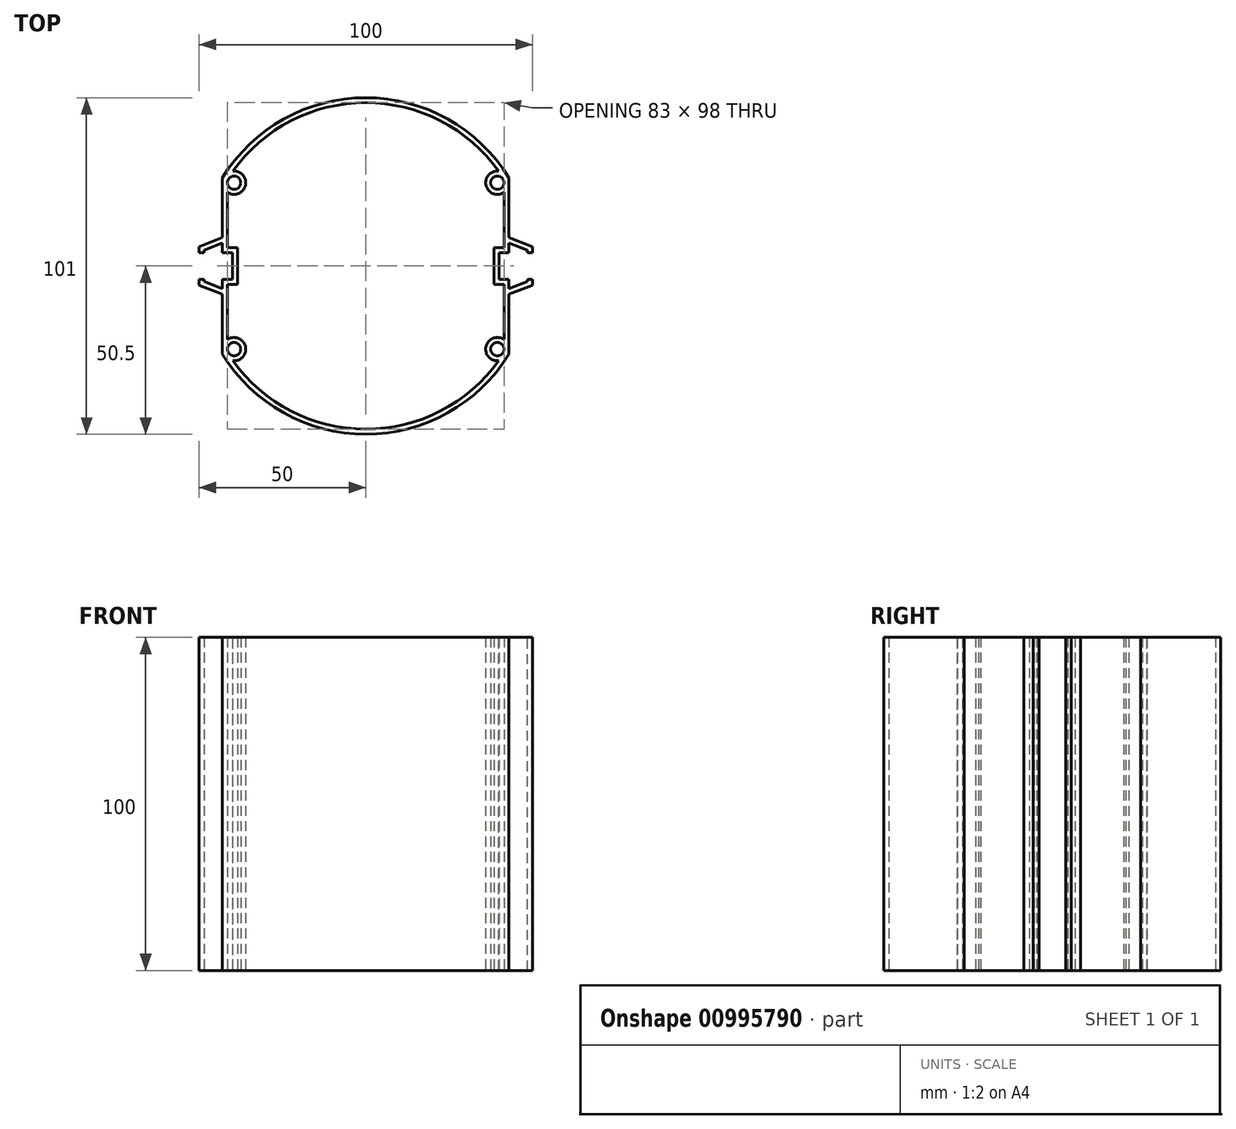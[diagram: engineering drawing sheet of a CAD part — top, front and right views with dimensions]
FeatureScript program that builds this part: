
annotation { "Feature Type Name" : "Feature", "Feature Type Description" : "" }
export const myFeature = defineFeature(function(context is Context, id is Id, definition is map)
    precondition{}
    {
        {
            var Q0;
            Q0=qCreatedBy(makeId("Top.planeOp"),FACE);
            var sketch = newSketch(context, id + "F0", { "sketchPlane" : qUnion([Q0])});
            skArc(sketch, "E0", {"start": v(43, 26.48) * mm, "mid": v(0, 50.5) * mm, "end": v(-43, 26.48) * mm});
            skArc(sketch, "E1", {"start": v(-43, -26.48) * mm, "mid": v(0, -50.5) * mm, "end": v(43, -26.48) * mm});
            skCircle(sketch, "E2", {"center": v(39.5, 24.98) * mm, "radius": 2 * mm});
            skCircle(sketch, "E3", {"center": v(-39.5, 24.98) * mm, "radius": 2 * mm});
            skCircle(sketch, "E4", {"center": v(-39.5, -24.98) * mm, "radius": 2 * mm});
            skCircle(sketch, "E5", {"center": v(39.5, -24.98) * mm, "radius": 2 * mm});
            skLineSegment(sketch, "E6.bottom", {"start": v(40, 4) * mm, "end": v(52, 4) * mm});
            skLineSegment(sketch, "E6.top", {"start": v(40, -4) * mm, "end": v(52, -4) * mm});
            skLineSegment(sketch, "E6.left", {"start": v(40, 4) * mm, "end": v(40, -4) * mm});
            skLineSegment(sketch, "E6.right", {"start": v(52, 4) * mm, "end": v(52, -4) * mm});
            skLineSegment(sketch, "E7", {"start": v(43, 26.48) * mm, "end": v(43, 4) * mm});
            skLineSegment(sketch, "E8", {"start": v(43, -26.48) * mm, "end": v(43, -4) * mm});
            skLineSegment(sketch, "E9.bottom", {"start": v(-40, 4) * mm, "end": v(-52, 4) * mm});
            skLineSegment(sketch, "E9.top", {"start": v(-40, -4) * mm, "end": v(-52, -4) * mm});
            skLineSegment(sketch, "E9.left", {"start": v(-40, 4) * mm, "end": v(-40, -4) * mm});
            skLineSegment(sketch, "E9.right", {"start": v(-52, 4) * mm, "end": v(-52, -4) * mm});
            skLineSegment(sketch, "E10", {"start": v(-43, 26.48) * mm, "end": v(-43, 4) * mm});
            skLineSegment(sketch, "E11", {"start": v(-43, -26.48) * mm, "end": v(-43, -4) * mm});
            skLineSegment(sketch, "E12.bottom", {"start": v(-50, 5.75) * mm, "end": v(-43, 5.75) * mm});
            skLineSegment(sketch, "E12.top", {"start": v(-50, -5.75) * mm, "end": v(-43, -5.75) * mm});
            skLineSegment(sketch, "E12.left", {"start": v(-50, 5.75) * mm, "end": v(-50, -5.75) * mm});
            skLineSegment(sketch, "E12.right", {"start": v(-43, 5.75) * mm, "end": v(-43, -5.75) * mm});
            skLineSegment(sketch, "E13", {"start": v(-50, 5.75) * mm, "end": v(-43, 8.5) * mm});
            skLineSegment(sketch, "E14", {"start": v(-50, -5.75) * mm, "end": v(-43, -8.5) * mm});
            skLineSegment(sketch, "E15.bottom", {"start": v(43, 5.75) * mm, "end": v(50, 5.75) * mm});
            skLineSegment(sketch, "E15.top", {"start": v(43, -5.75) * mm, "end": v(50, -5.75) * mm});
            skLineSegment(sketch, "E15.left", {"start": v(43, 5.75) * mm, "end": v(43, -5.75) * mm});
            skLineSegment(sketch, "E15.right", {"start": v(50, 5.75) * mm, "end": v(50, -5.75) * mm});
            skLineSegment(sketch, "E16", {"start": v(50, 5.75) * mm, "end": v(43, 8.5) * mm});
            skLineSegment(sketch, "E17", {"start": v(50, -5.75) * mm, "end": v(43, -8.5) * mm});
            skSolve(sketch);
        }
        {
            var Q0;
            Q0=makeQuery(id+"F0.imprint","IMPRINT",FACE,{"disambiguationData":[TD([[makeQuery(id+"F0.imprint","IMPRINT",EDGE,{"derivedFrom":sQuery(id+"F0.wireOp",EDGE,"E0")}),1.0]])]});
            extrude(context, id + "F1", {"entities" : qUnion([Q0]), "depth" : 100 * mm, "offsetDistance" : 25 * mm, "hasSecondDirection" : true, "secondDirectionOppositeDirection" : true, "secondDirectionDepth" : 1.5 * mm});
        }
        {
            var Q0;
            Q0=makeQuery(id+"F1.opExtrude","CAP_FACE",FACE,{"disambiguationData":[OSD([sQuery(id+"F0.wireOp",EDGE,"E0"),sQuery(id+"F0.wireOp",EDGE,"E1"),sQuery(id+"F0.wireOp",EDGE,"E2"),sQuery(id+"F0.wireOp",EDGE,"E3"),sQuery(id+"F0.wireOp",EDGE,"E4"),sQuery(id+"F0.wireOp",EDGE,"E5"),sQuery(id+"F0.wireOp",EDGE,"E6.bottom"),sQuery(id+"F0.wireOp",EDGE,"E6.top"),sQuery(id+"F0.wireOp",EDGE,"E6.left"),sQuery(id+"F0.wireOp",EDGE,"E7"),sQuery(id+"F0.wireOp",EDGE,"E8"),sQuery(id+"F0.wireOp",EDGE,"E9.bottom"),sQuery(id+"F0.wireOp",EDGE,"E9.top"),sQuery(id+"F0.wireOp",EDGE,"E9.left"),sQuery(id+"F0.wireOp",EDGE,"E10"),sQuery(id+"F0.wireOp",EDGE,"E11")])],"isStart":false});
            shell(context, id + "F2", {"entities" : qUnion([Q0]), "thickness" : 1.5 * mm});
        }
        {
            var Q0;
            {var subQ0=sQuery(id+"F0.wireOp",EDGE,"E12.bottom");Q0=makeQuery(id+"F0.imprint","IMPRINT",FACE,{"disambiguationData":[TD([[makeQuery(id+"F0.imprint","IMPRINT",EDGE,{"derivedFrom":subQ0}),1.0]])]});}
            var Q1;
            {var subQ5=sQuery(id+"F0.wireOp",EDGE,"E12.bottom");Q1=makeQuery(id+"F0.imprint","IMPRINT",FACE,{"disambiguationData":[TD([[makeQuery(id+"F0.imprint","IMPRINT",EDGE,{"derivedFrom":subQ5}),-1.0]])]});}
            var Q2;
            {var subQ0=sQuery(id+"F0.wireOp",EDGE,"E12.left");var subQ1=sQuery(id+"F0.wireOp",EDGE,"E9.bottom");var subQ2=makeQuery(id+"F0.imprint","INTERSECT",VERTEX,{"derivedFrom":[subQ1,subQ0]});Q2=makeQuery(id+"F0.imprint","IMPRINT",FACE,{"disambiguationData":[TD([[makeQuery(id+"F0.imprint","IMPRINT",EDGE,{"disambiguationData":[TD([[subQ2,1.0]])],"derivedFrom":subQ1}),1.0]])]});}
            var Q3;
            {var subQ5=sQuery(id+"F0.wireOp",EDGE,"E12.top");Q3=makeQuery(id+"F0.imprint","IMPRINT",FACE,{"disambiguationData":[TD([[makeQuery(id+"F0.imprint","IMPRINT",EDGE,{"derivedFrom":subQ5}),1.0]])]});}
            var Q4;
            {var subQ0=sQuery(id+"F0.wireOp",EDGE,"E12.top");Q4=makeQuery(id+"F0.imprint","IMPRINT",FACE,{"disambiguationData":[TD([[makeQuery(id+"F0.imprint","IMPRINT",EDGE,{"derivedFrom":subQ0}),-1.0]])]});}
            var Q5;
            {var subQ0=sQuery(id+"F0.wireOp",EDGE,"E9.left");Q5=makeQuery(id+"F0.imprint","IMPRINT",FACE,{"disambiguationData":[TD([[makeQuery(id+"F0.imprint","IMPRINT",EDGE,{"derivedFrom":subQ0}),-1.0]])]});}
            var Q6;
            {var subQ0=sQuery(id+"F0.wireOp",EDGE,"E15.top");Q6=makeQuery(id+"F0.imprint","IMPRINT",FACE,{"disambiguationData":[TD([[makeQuery(id+"F0.imprint","IMPRINT",EDGE,{"derivedFrom":subQ0}),-1.0]])]});}
            var Q7;
            {var subQ5=sQuery(id+"F0.wireOp",EDGE,"E15.top");Q7=makeQuery(id+"F0.imprint","IMPRINT",FACE,{"disambiguationData":[TD([[makeQuery(id+"F0.imprint","IMPRINT",EDGE,{"derivedFrom":subQ5}),1.0]])]});}
            var Q8;
            {var subQ0=sQuery(id+"F0.wireOp",EDGE,"E15.right");var subQ1=sQuery(id+"F0.wireOp",EDGE,"E6.bottom");var subQ2=makeQuery(id+"F0.imprint","INTERSECT",VERTEX,{"derivedFrom":[subQ1,subQ0]});Q8=makeQuery(id+"F0.imprint","IMPRINT",FACE,{"disambiguationData":[TD([[makeQuery(id+"F0.imprint","IMPRINT",EDGE,{"disambiguationData":[TD([[subQ2,1.0]])],"derivedFrom":subQ1}),-1.0]])]});}
            var Q9;
            {var subQ0=sQuery(id+"F0.wireOp",EDGE,"E6.left");Q9=makeQuery(id+"F0.imprint","IMPRINT",FACE,{"disambiguationData":[TD([[makeQuery(id+"F0.imprint","IMPRINT",EDGE,{"derivedFrom":subQ0}),1.0]])]});}
            var Q10;
            {var subQ0=sQuery(id+"F0.wireOp",EDGE,"E15.bottom");Q10=makeQuery(id+"F0.imprint","IMPRINT",FACE,{"disambiguationData":[TD([[makeQuery(id+"F0.imprint","IMPRINT",EDGE,{"derivedFrom":subQ0}),1.0]])]});}
            var Q11;
            {var subQ5=sQuery(id+"F0.wireOp",EDGE,"E15.bottom");Q11=makeQuery(id+"F0.imprint","IMPRINT",FACE,{"disambiguationData":[TD([[makeQuery(id+"F0.imprint","IMPRINT",EDGE,{"derivedFrom":subQ5}),-1.0]])]});}
            extrude(context, id + "F3", {"entities" : qUnion([Q0, Q1, Q2, Q3, Q4, Q5, Q6, Q7, Q8, Q9, Q10, Q11]), "operationType" : NewBodyOperationType.ADD, "depth" : 100 * mm, "offsetDistance" : 25 * mm, "hasSecondDirection" : true, "secondDirectionOppositeDirection" : true, "secondDirectionDepth" : 1.5 * mm});
        }
        {
            var Q0;
            {var subQ0=sQuery(id+"F0.wireOp",EDGE,"E12.right");var subQ1=sQuery(id+"F0.wireOp",EDGE,"E11");var subQ2=sQuery(id+"F0.wireOp",EDGE,"E10");var subQ3=sQuery(id+"F0.wireOp",EDGE,"E9.left");var subQ4=sQuery(id+"F0.wireOp",EDGE,"E9.top");var subQ5=sQuery(id+"F0.wireOp",EDGE,"E9.bottom");Q0=makeQuery(id+"F3.boolean.opBoolean","MERGE",FACE,{"derivedFrom":[makeQuery(id+"F1.opExtrude","CAP_FACE",FACE,{"disambiguationData":[OSD([sQuery(id+"F0.wireOp",EDGE,"E0"),sQuery(id+"F0.wireOp",EDGE,"E1"),sQuery(id+"F0.wireOp",EDGE,"E2"),sQuery(id+"F0.wireOp",EDGE,"E3"),sQuery(id+"F0.wireOp",EDGE,"E4"),sQuery(id+"F0.wireOp",EDGE,"E5"),sQuery(id+"F0.wireOp",EDGE,"E6.bottom"),sQuery(id+"F0.wireOp",EDGE,"E6.top"),sQuery(id+"F0.wireOp",EDGE,"E6.left"),sQuery(id+"F0.wireOp",EDGE,"E7"),sQuery(id+"F0.wireOp",EDGE,"E8"),subQ5,subQ4,subQ3,subQ2,subQ1,subQ0])],"isStart":false}),makeQuery(id+"F3.opExtrude","CAP_FACE",FACE,{"disambiguationData":[OSD([subQ5,subQ4,subQ3,subQ2,subQ1,sQuery(id+"F0.wireOp",EDGE,"E12.left"),subQ0,sQuery(id+"F0.wireOp",EDGE,"E13"),sQuery(id+"F0.wireOp",EDGE,"E14")])],"isStart":false})]});}
            shell(context, id + "F4", {"entities" : qUnion([Q0]), "thickness" : 1.5 * mm});
        }
        {
            var Q0;
            {var subQ0=sQuery(id+"F0.wireOp",EDGE,"E9.right");Q0=makeQuery(id+"F0.imprint","IMPRINT",FACE,{"disambiguationData":[TD([[makeQuery(id+"F0.imprint","IMPRINT",EDGE,{"derivedFrom":subQ0}),1.0]])]});}
            var Q1;
            {var subQ0=sQuery(id+"F0.wireOp",EDGE,"E12.left");var subQ1=sQuery(id+"F0.wireOp",EDGE,"E9.bottom");var subQ2=makeQuery(id+"F0.imprint","INTERSECT",VERTEX,{"derivedFrom":[subQ1,subQ0]});Q1=makeQuery(id+"F0.imprint","IMPRINT",FACE,{"disambiguationData":[TD([[makeQuery(id+"F0.imprint","IMPRINT",EDGE,{"disambiguationData":[TD([[subQ2,1.0]])],"derivedFrom":subQ1}),1.0]])]});}
            var Q2;
            {var subQ5=sQuery(id+"F0.wireOp",EDGE,"E12.bottom");Q2=makeQuery(id+"F0.imprint","IMPRINT",FACE,{"disambiguationData":[TD([[makeQuery(id+"F0.imprint","IMPRINT",EDGE,{"derivedFrom":subQ5}),-1.0]])]});}
            var Q3;
            {var subQ0=sQuery(id+"F0.wireOp",EDGE,"E12.bottom");Q3=makeQuery(id+"F0.imprint","IMPRINT",FACE,{"disambiguationData":[TD([[makeQuery(id+"F0.imprint","IMPRINT",EDGE,{"derivedFrom":subQ0}),1.0]])]});}
            var Q4;
            {var subQ0=sQuery(id+"F0.wireOp",EDGE,"E9.left");Q4=makeQuery(id+"F0.imprint","IMPRINT",FACE,{"disambiguationData":[TD([[makeQuery(id+"F0.imprint","IMPRINT",EDGE,{"derivedFrom":subQ0}),-1.0]])]});}
            var Q5;
            {var subQ0=sQuery(id+"F0.wireOp",EDGE,"E12.top");Q5=makeQuery(id+"F0.imprint","IMPRINT",FACE,{"disambiguationData":[TD([[makeQuery(id+"F0.imprint","IMPRINT",EDGE,{"derivedFrom":subQ0}),-1.0]])]});}
            var Q6;
            {var subQ15=sQuery(id+"F0.wireOp",EDGE,"E0");Q6=makeQuery(id+"F0.imprint","IMPRINT",FACE,{"disambiguationData":[TD([[makeQuery(id+"F0.imprint","IMPRINT",EDGE,{"derivedFrom":subQ15}),1.0]])]});}
            var Q7;
            {var subQ0=sQuery(id+"F0.wireOp",EDGE,"E6.left");Q7=makeQuery(id+"F0.imprint","IMPRINT",FACE,{"disambiguationData":[TD([[makeQuery(id+"F0.imprint","IMPRINT",EDGE,{"derivedFrom":subQ0}),1.0]])]});}
            var Q8;
            {var subQ0=sQuery(id+"F0.wireOp",EDGE,"E15.right");var subQ1=sQuery(id+"F0.wireOp",EDGE,"E6.bottom");var subQ2=makeQuery(id+"F0.imprint","INTERSECT",VERTEX,{"derivedFrom":[subQ1,subQ0]});Q8=makeQuery(id+"F0.imprint","IMPRINT",FACE,{"disambiguationData":[TD([[makeQuery(id+"F0.imprint","IMPRINT",EDGE,{"disambiguationData":[TD([[subQ2,1.0]])],"derivedFrom":subQ1}),-1.0]])]});}
            var Q9;
            {var subQ5=sQuery(id+"F0.wireOp",EDGE,"E15.bottom");Q9=makeQuery(id+"F0.imprint","IMPRINT",FACE,{"disambiguationData":[TD([[makeQuery(id+"F0.imprint","IMPRINT",EDGE,{"derivedFrom":subQ5}),-1.0]])]});}
            var Q10;
            {var subQ0=sQuery(id+"F0.wireOp",EDGE,"E15.bottom");Q10=makeQuery(id+"F0.imprint","IMPRINT",FACE,{"disambiguationData":[TD([[makeQuery(id+"F0.imprint","IMPRINT",EDGE,{"derivedFrom":subQ0}),1.0]])]});}
            var Q11;
            {var subQ0=sQuery(id+"F0.wireOp",EDGE,"E15.top");Q11=makeQuery(id+"F0.imprint","IMPRINT",FACE,{"disambiguationData":[TD([[makeQuery(id+"F0.imprint","IMPRINT",EDGE,{"derivedFrom":subQ0}),-1.0]])]});}
            var Q12;
            {var subQ5=sQuery(id+"F0.wireOp",EDGE,"E15.top");Q12=makeQuery(id+"F0.imprint","IMPRINT",FACE,{"disambiguationData":[TD([[makeQuery(id+"F0.imprint","IMPRINT",EDGE,{"derivedFrom":subQ5}),1.0]])]});}
            var Q13;
            {var subQ0=sQuery(id+"F0.wireOp",EDGE,"E6.right");Q13=makeQuery(id+"F0.imprint","IMPRINT",FACE,{"disambiguationData":[TD([[makeQuery(id+"F0.imprint","IMPRINT",EDGE,{"derivedFrom":subQ0}),-1.0]])]});}
            var Q14;
            {var subQ5=sQuery(id+"F0.wireOp",EDGE,"E12.top");Q14=makeQuery(id+"F0.imprint","IMPRINT",FACE,{"disambiguationData":[TD([[makeQuery(id+"F0.imprint","IMPRINT",EDGE,{"derivedFrom":subQ5}),1.0]])]});}
            var Q15;
            Q15=makeQuery(id+"F0.imprint","IMPRINT",FACE,{"disambiguationData":[TD([[makeQuery(id+"F0.imprint","IMPRINT",EDGE,{"derivedFrom":sQuery(id+"F0.wireOp",EDGE,"E3")}),1.0]])]});
            var Q16;
            Q16=makeQuery(id+"F0.imprint","IMPRINT",FACE,{"disambiguationData":[TD([[makeQuery(id+"F0.imprint","IMPRINT",EDGE,{"derivedFrom":sQuery(id+"F0.wireOp",EDGE,"E2")}),1.0]])]});
            var Q17;
            Q17=makeQuery(id+"F0.imprint","IMPRINT",FACE,{"disambiguationData":[TD([[makeQuery(id+"F0.imprint","IMPRINT",EDGE,{"derivedFrom":sQuery(id+"F0.wireOp",EDGE,"E5")}),1.0]])]});
            var Q18;
            Q18=makeQuery(id+"F0.imprint","IMPRINT",FACE,{"disambiguationData":[TD([[makeQuery(id+"F0.imprint","IMPRINT",EDGE,{"derivedFrom":sQuery(id+"F0.wireOp",EDGE,"E4")}),1.0]])]});
            extrude(context, id + "F5", {"entities" : qUnion([Q0, Q1, Q2, Q3, Q4, Q5, Q6, Q7, Q8, Q9, Q10, Q11, Q12, Q13, Q14, Q15, Q16, Q17, Q18]), "operationType" : NewBodyOperationType.REMOVE, "oppositeDirection" : true, "depth" : 1.5 * mm, "offsetDistance" : 25 * mm});
        }
        {
            var Q0;
            {var subQ0=sQuery(id+"F0.wireOp",EDGE,"E12.left");var subQ1=sQuery(id+"F0.wireOp",EDGE,"E9.bottom");var subQ2=makeQuery(id+"F0.imprint","INTERSECT",VERTEX,{"derivedFrom":[subQ1,subQ0]});Q0=makeQuery(id+"F0.imprint","IMPRINT",FACE,{"disambiguationData":[TD([[makeQuery(id+"F0.imprint","IMPRINT",EDGE,{"disambiguationData":[TD([[subQ2,1.0]])],"derivedFrom":subQ1}),1.0]])]});}
            var Q1;
            {var subQ0=sQuery(id+"F0.wireOp",EDGE,"E15.right");var subQ1=sQuery(id+"F0.wireOp",EDGE,"E6.bottom");var subQ2=makeQuery(id+"F0.imprint","INTERSECT",VERTEX,{"derivedFrom":[subQ1,subQ0]});Q1=makeQuery(id+"F0.imprint","IMPRINT",FACE,{"disambiguationData":[TD([[makeQuery(id+"F0.imprint","IMPRINT",EDGE,{"disambiguationData":[TD([[subQ2,1.0]])],"derivedFrom":subQ1}),-1.0]])]});}
            extrude(context, id + "F6", {"entities" : qUnion([Q0, Q1]), "operationType" : NewBodyOperationType.REMOVE, "depth" : 100 * mm, "offsetDistance" : 25 * mm, "hasSecondDirection" : true, "secondDirectionOppositeDirection" : true, "secondDirectionDepth" : 1.5 * mm});
        }
    });
